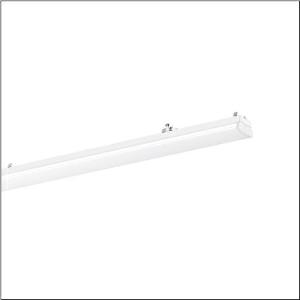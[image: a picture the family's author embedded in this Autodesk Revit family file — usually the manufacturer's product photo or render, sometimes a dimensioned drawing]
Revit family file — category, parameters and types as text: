
# Revit family: licross_r__11_recessed_opal_ho_51tl1ddn46xm_4fcf
name_source: partatom
category: Lighting Fixtures
units: mm (PartAtom-declared; Revit-internal decimal feet)

## family parameters
Cut with Voids When Loaded = No
Host = Face
Light Source = No
Part Type = Normal
Room Calculation Point = No
Round Connector Dimension = Use Diameter
Shared = No

## types (1)
- --- (1 x LED, 6320 lm, 33.5 W, 4000K)
    Apparent Load = 34 VA
    CIE Flux Codes = 44 73 91 87 100
    Color Rendering = 80
    Color Temperature = 4000K
    Default Elevation = 1800 mm
    Description = Licross® 11 recessed opal HO, luminaire insert, of sheet steel, coil coated, white, length: 1.500mm, width: 76mm, height: 87mm, LED rated luminous flux: 6.320lm, light colour: 840, control gear: DALI 2, with plug, 5-pole, with phase selection, mains connection: 220..240V, AC, 50/60Hz, rated input power: 34W, halogen-free wiring, primary optical cover: cover, of PMMA, light emission: direct with ceiling illumination distribution, primary light characteristic: symmetric, protection rating (complete): IP40, insulation class (complete): insulation class I (protective earthing), certification: CE, ENEC, VDE, UKCA, protection symbol: D if used in an environment without relevant dust loads with corresponding accessories, impact resistance: IK06, permissible ambient temperature for indoor applications: -25..+45°C, corresponds to IFS (International Featured Standards) requirements for safety and quality in the food industry, reducing of maximum allowable ambient temperature of 5°C with ceiling mounting, LABS conformity tested according to VDMA 24364:2018-05, packaging unit: 1 piece
    Height = 83 mm
    Lamp = 1 x LED
    Lamp Light Flux = 6320 lm
    Lamp Power = 33.5 W
    Lamp count = 1
    Length = 1500 mm
    Luminous efficacy = 189 lm/W
    Manufacturer = Siteco
    ModVariant = No
    Model = 51TL1DDN46XM
    Mounting Place = Ceiling
    Mounting Type = Pendant
    Number of Poles = 1
    OnlyDefault = Yes
    Power Factor = 1
    Product Name = Licross® 11 recessed opal HO
    Product group = luminaire insert
    ProductGroupID = 901
    Protection Class = Protection class I
    Protection Degree = IP 40
    RLX_Detail_Level = 1
    RLX_Emergency_Light_Flux = 0 lm
    RLX_Emergency_Type = 0
    RLX_Emergency_Type_DB = No
    RlxData = <blob elided: 18005 chars, md5=dc96adda>
    Socket = socket
    Standby Power = 0 W
    System Light Flux = 6320 lm
    System Power = 34 W
    Type Comments = factory setting: luminous flux: 100 % | dim-lin: 254 | 232 mA
    Type Image = l_1313666.jpg
    URL = http://relux.com
    VarID = @adj_027349
    Voltage = 0 V
    Weight = 0.00 kg
    Width = 76 mm

## geometry (parser evidence)
native form markers: Blend x4, Sweep x12
no freeform markers — native parametric forms only
